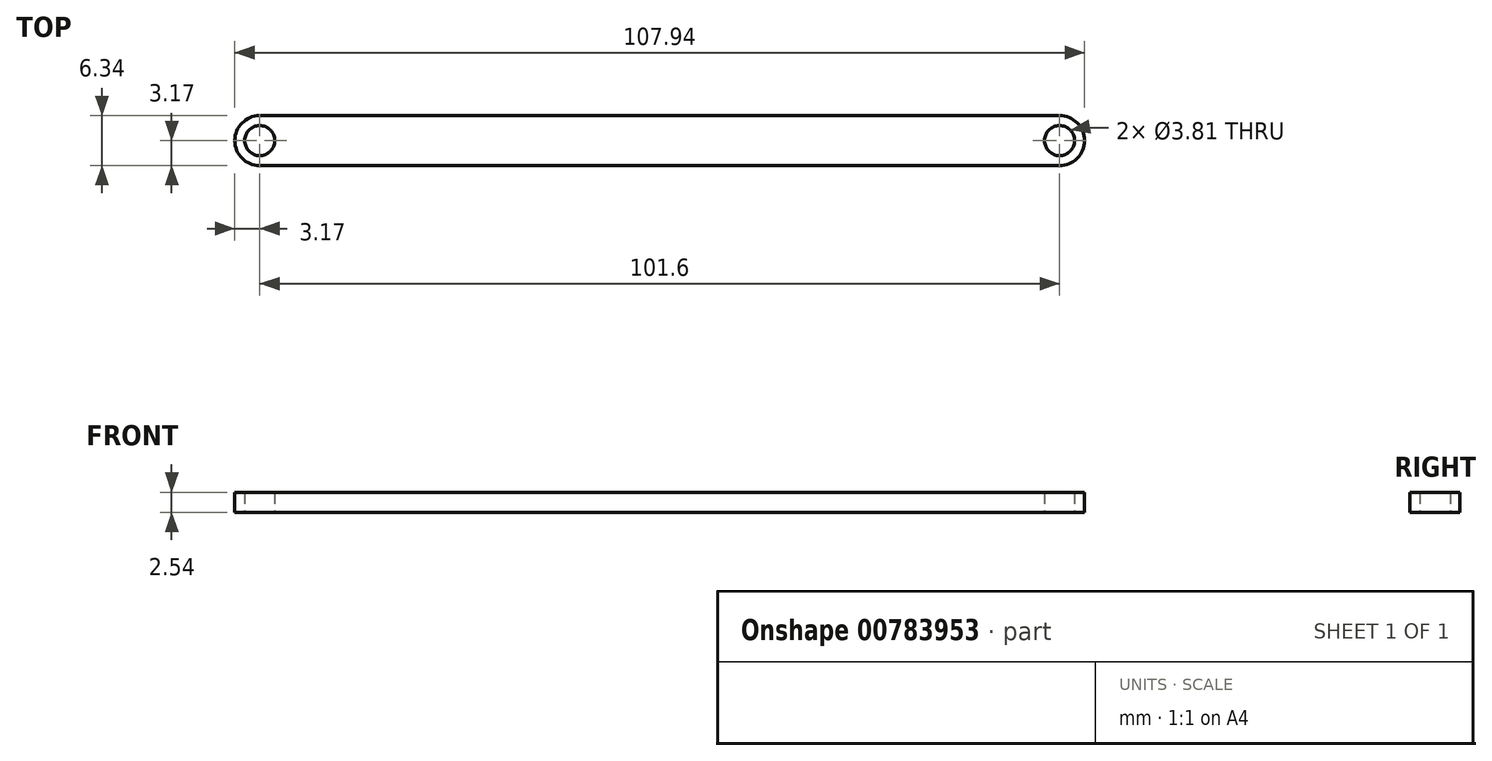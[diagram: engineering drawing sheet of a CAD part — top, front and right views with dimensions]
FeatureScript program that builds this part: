
annotation { "Feature Type Name" : "Feature", "Feature Type Description" : "" }
export const myFeature = defineFeature(function(context is Context, id is Id, definition is map)
    precondition{}
    {
        {
            var Q0;
            Q0=qCreatedBy(makeId("Top.planeOp"),FACE);
            var sketch = newSketch(context, id + "F0", { "sketchPlane" : qUnion([Q0])});
            skCircle(sketch, "E0", {"center": v(0, 0) * mm, "radius": 1.9 * mm});
            skCircle(sketch, "E1", {"center": v(0, 0) * mm, "radius": 3.18 * mm});
            skLineSegment(sketch, "E2", {"start": v(0, 3.18) * mm, "end": v(101.6, 3.18) * mm});
            skCircle(sketch, "E3", {"center": v(101.6, 0) * mm, "radius": 1.9 * mm});
            skCircle(sketch, "E4", {"center": v(101.6, 0) * mm, "radius": 3.17 * mm});
            skLineSegment(sketch, "E5", {"start": v(0, -3.17) * mm, "end": v(101.6, -3.17) * mm});
            skSolve(sketch);
        }
        {
            var Q0;
            Q0 = qSketchRegion(id + "F0", true);
            extrude(context, id + "F1", {"entities" : qUnion([Q0]), "depth" : 2.54 * mm, "offsetDistance" : 25.4 * mm});
        }
    });
